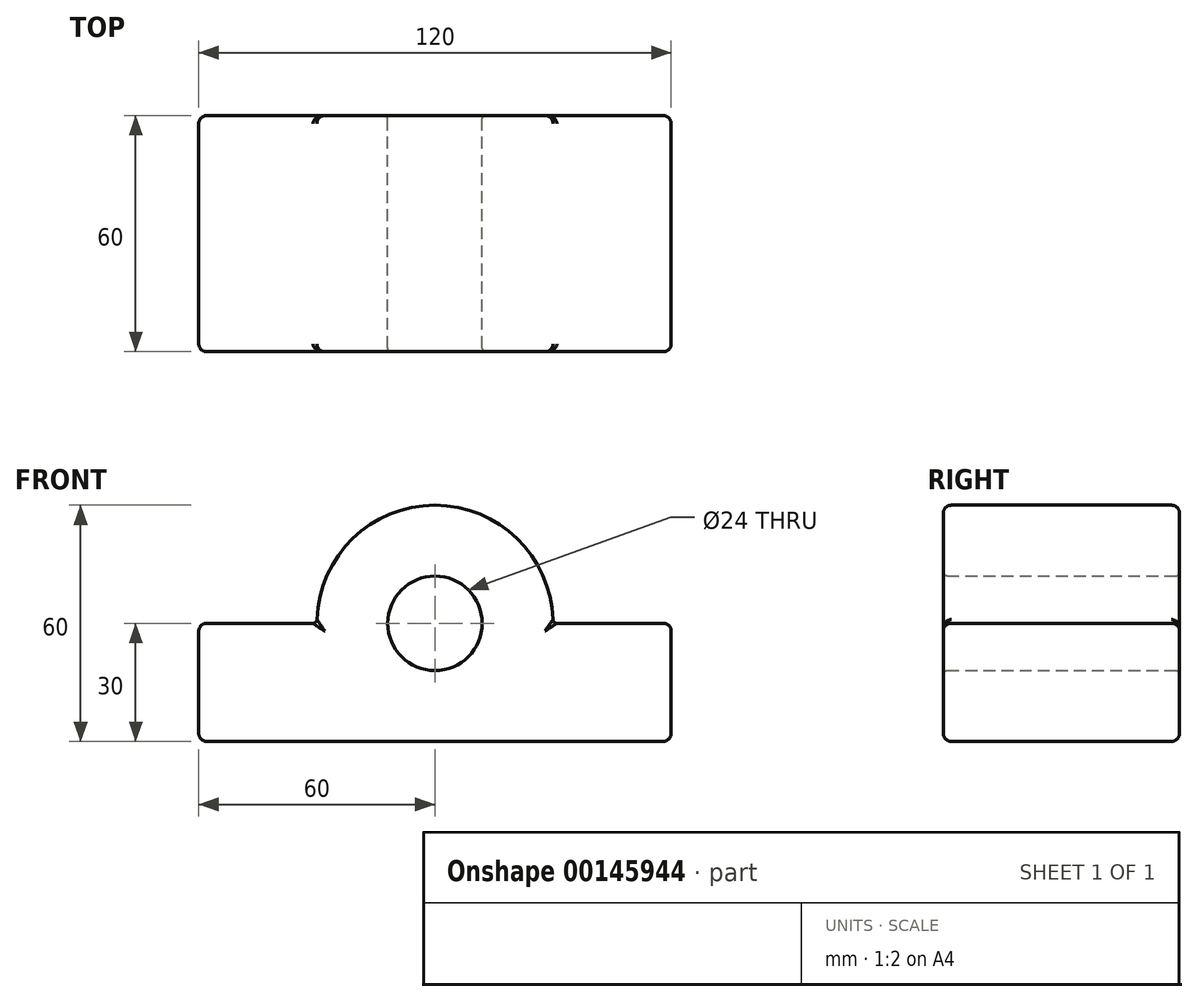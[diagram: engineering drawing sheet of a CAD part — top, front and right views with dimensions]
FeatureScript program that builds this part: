
annotation { "Feature Type Name" : "Feature", "Feature Type Description" : "" }
export const myFeature = defineFeature(function(context is Context, id is Id, definition is map)
    precondition{}
    {
        {
            var Q0;
            Q0=qCreatedBy(makeId("Front.planeOp"),FACE);
            var sketch = newSketch(context, id + "F0", { "sketchPlane" : qUnion([Q0])});
            skLineSegment(sketch, "E0", {"start": v(0, 0) * mm, "end": v(120, 0) * mm});
            skLineSegment(sketch, "E1", {"start": v(120, 0) * mm, "end": v(120, 30) * mm});
            skLineSegment(sketch, "E2", {"start": v(120, 30) * mm, "end": v(90, 30) * mm});
            skLineSegment(sketch, "E3", {"start": v(0, 0) * mm, "end": v(0, 30) * mm});
            skLineSegment(sketch, "E4", {"start": v(0, 30) * mm, "end": v(30, 30) * mm});
            skArc(sketch, "E5", {"start": v(90, 30) * mm, "mid": v(60, 60) * mm, "end": v(30, 30) * mm});
            skCircle(sketch, "E6", {"center": v(60, 30) * mm, "radius": 12 * mm});
            skSolve(sketch);
        }
        {
            var Q0;
            Q0=makeQuery(id+"F0.imprint","IMPRINT",FACE,{"disambiguationData":[TD([[makeQuery(id+"F0.imprint","IMPRINT",EDGE,{"derivedFrom":sQuery(id+"F0.wireOp",EDGE,"E0")}),1.0]])]});
            extrude(context, id + "F1", {"entities" : qUnion([Q0]), "depth" : 60 * mm});
        }
        {
            var Q0;
            Q0=makeQuery(id+"F1.opExtrude","CAP_EDGE",EDGE,{"disambiguationData":[OSD([sQuery(id+"F0.wireOp",EDGE,"E4")])],"isStart":false});
            var Q1;
            Q1=makeQuery(id+"F1.opExtrude","CAP_EDGE",EDGE,{"disambiguationData":[OSD([sQuery(id+"F0.wireOp",EDGE,"E3")])],"isStart":false});
            var Q2;
            Q2=makeQuery(id+"F1.opExtrude","CAP_EDGE",EDGE,{"disambiguationData":[OSD([sQuery(id+"F0.wireOp",EDGE,"E0")])],"isStart":false});
            var Q3;
            Q3=makeQuery(id+"F1.opExtrude","CAP_EDGE",EDGE,{"disambiguationData":[OSD([sQuery(id+"F0.wireOp",EDGE,"E1")])],"isStart":false});
            var Q4;
            Q4=makeQuery(id+"F1.opExtrude","CAP_EDGE",EDGE,{"disambiguationData":[OSD([sQuery(id+"F0.wireOp",EDGE,"E2")])],"isStart":false});
            var Q5;
            Q5=makeQuery(id+"F1.opExtrude","CAP_EDGE",EDGE,{"disambiguationData":[OSD([sQuery(id+"F0.wireOp",EDGE,"E5")])],"isStart":false});
            var Q6;
            Q6=makeQuery(id+"F1.opExtrude","CAP_EDGE",EDGE,{"disambiguationData":[OSD([sQuery(id+"F0.wireOp",EDGE,"E5")])],"isStart":true});
            var Q7;
            Q7=makeQuery(id+"F1.opExtrude","CAP_EDGE",EDGE,{"disambiguationData":[OSD([sQuery(id+"F0.wireOp",EDGE,"E4")])],"isStart":true});
            var Q8;
            Q8=makeQuery(id+"F1.opExtrude","CAP_EDGE",EDGE,{"disambiguationData":[OSD([sQuery(id+"F0.wireOp",EDGE,"E3")])],"isStart":true});
            var Q9;
            Q9=makeQuery(id+"F1.opExtrude","CAP_EDGE",EDGE,{"disambiguationData":[OSD([sQuery(id+"F0.wireOp",EDGE,"E0")])],"isStart":true});
            var Q10;
            Q10=makeQuery(id+"F1.opExtrude","CAP_EDGE",EDGE,{"disambiguationData":[OSD([sQuery(id+"F0.wireOp",EDGE,"E2")])],"isStart":true});
            var Q11;
            Q11=makeQuery(id+"F1.opExtrude","CAP_EDGE",EDGE,{"disambiguationData":[OSD([sQuery(id+"F0.wireOp",EDGE,"E1")])],"isStart":true});
            var Q12;
            Q12=makeQuery(id+"F1.opExtrude","SWEPT_EDGE",EDGE,{"disambiguationData":[OSD([sQuery(id+"F0.wireOp",EDGE,"E1"),sQuery(id+"F0.wireOp",EDGE,"E2")])]});
            var Q13;
            Q13=makeQuery(id+"F1.opExtrude","SWEPT_EDGE",EDGE,{"disambiguationData":[OSD([sQuery(id+"F0.wireOp",EDGE,"E3"),sQuery(id+"F0.wireOp",EDGE,"E4")])]});
            var Q14;
            Q14=makeQuery(id+"F1.opExtrude","SWEPT_EDGE",EDGE,{"disambiguationData":[OSD([sQuery(id+"F0.wireOp",EDGE,"E0"),sQuery(id+"F0.wireOp",EDGE,"E1")])]});
            var Q15;
            Q15=makeQuery(id+"F1.opExtrude","SWEPT_EDGE",EDGE,{"disambiguationData":[OSD([sQuery(id+"F0.wireOp",EDGE,"E0"),sQuery(id+"F0.wireOp",EDGE,"E3")])]});
            fillet(context, id + "F2", {"entities" : qUnion([Q0, Q1, Q2, Q3, Q4, Q5, Q6, Q7, Q8, Q9, Q10, Q11, Q12, Q13, Q14, Q15]), "radius" : 2 * mm, "tangentPropagation" : true, "allowEdgeOverflow" : false});
        }
        {
            var Q0;
            Q0=makeQuery(id+"F1.opExtrude","CAP_EDGE",EDGE,{"disambiguationData":[OSD([sQuery(id+"F0.wireOp",EDGE,"E6")])],"isStart":false});
            var Q1;
            Q1=makeQuery(id+"F1.opExtrude","CAP_EDGE",EDGE,{"disambiguationData":[OSD([sQuery(id+"F0.wireOp",EDGE,"E6")])],"isStart":true});
            var Q2;
            Q2=makeQuery(id+"F1.opExtrude","SWEPT_EDGE",EDGE,{"disambiguationData":[OSD([sQuery(id+"F0.wireOp",EDGE,"E2"),sQuery(id+"F0.wireOp",EDGE,"E5")])]});
            var Q3;
            Q3=makeQuery(id+"F1.opExtrude","SWEPT_EDGE",EDGE,{"disambiguationData":[OSD([sQuery(id+"F0.wireOp",EDGE,"E4"),sQuery(id+"F0.wireOp",EDGE,"E5")])]});
            fillet(context, id + "F3", {"entities" : qUnion([Q0, Q1, Q2, Q3]), "radius" : 1 * mm, "tangentPropagation" : true, "allowEdgeOverflow" : false});
        }
    });
